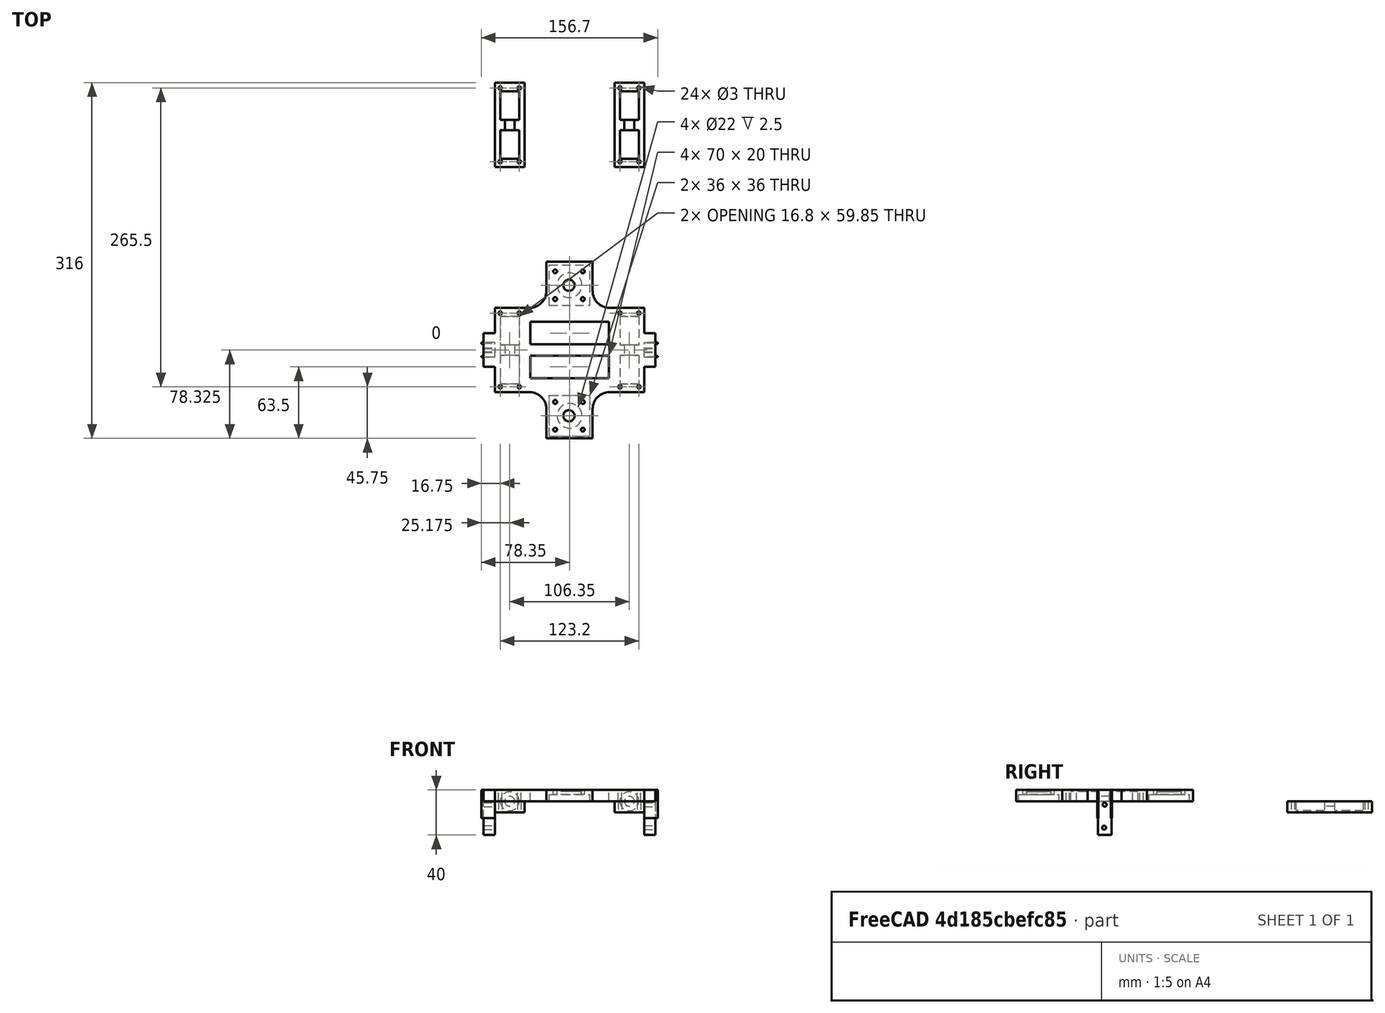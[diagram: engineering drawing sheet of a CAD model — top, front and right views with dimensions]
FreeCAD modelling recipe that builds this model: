
FCSTD DOCUMENT  (FreeCAD 0.16R6712 (Git))
Label: 1.3
License: All rights reserved
LicenseURL: http://en.wikipedia.org/wiki/All_rights_reserved
objects: Part::Cut×24, Part::Cylinder×23, Part::Box×14, Part::MultiFuse×7, Part::FeaturePython×4, Part::Fillet×4, Part::Fuse×2, Part::Feature×2
note: 80 computed .brp shape members not serialized (recipe doc carries the construction recipe); baked Part::Feature solids carry a one-line shape summary decoded from their .brp

FEATURE [Part::Box] Box  label="Cubo"
  Height = 10
  Length = 26.35
  Width = 75
FEATURE [Part::Cylinder] Cylinder  label="Cilindro"
  Angle = 360
  Height = 10
  Placement = pos=(4.75,4.75,0) rot=(0,0,1;0rad)
  Radius = 1.5
FEATURE [Part::Cylinder] Cylinder002  label="Cilindro002"
  Angle = 360
  Height = 10
  Placement = pos=(4.75,70.25,0) rot=(0,0,1;0rad)
  Radius = 1.5
FEATURE [Part::Cylinder] Cylinder003  label="Cilindro003"
  Angle = 360
  Height = 10
  Placement = pos=(21.6,4.75,0) rot=(0,0,1;0rad)
  Radius = 1.5
FEATURE [Part::Cut] Cut
  Base = -> Box
  Tool = -> Cylinder
FEATURE [Part::Cut] Cut001
  Base = -> Cut
  Tool = -> Cylinder002
FEATURE [Part::Cylinder] Cylinder004  label="Cilindro004"
  Angle = 360
  Height = 25.35
  Placement = pos=(13.175,30,0) rot=(1,0,0;1.5708rad)
  Radius = 8.4
FEATURE [Part::Cylinder] Cylinder005  label="Cilindro005"
  Angle = 360
  Height = 25.35
  Placement = pos=(13.175,64.5,0) rot=(1,0,0;1.5708rad)
  Radius = 8.4
FEATURE [Part::Cylinder] Cylinder006  label="Cilindro006"
  Angle = 360
  Height = 9.5
  Placement = pos=(13.175,39.5,0) rot=(1,0,0;1.5708rad)
  Radius = 4.4
FEATURE [Part::Fuse] Fusion
  Base = -> Cylinder004
  Tool = -> Cylinder005
FEATURE [Part::Fuse] Fusion001
  Base = -> Fusion
  Placement = pos=(0,2.75,0) rot=(0,0,1;0rad)
  Tool = -> Cylinder006
FEATURE [Part::Box] Box001  label="Centro"
  Height = 10
  Length = 80
  Placement = pos=(26.35,0,0) rot=(0,0,1;0rad)
  Width = 75
FEATURE [Part::Box] Box002  label="Lucernario"
  Height = 10
  Length = 70
  Placement = pos=(31.35,12.5,0) rot=(0,0,1;0rad)
  Width = 20
FEATURE [Part::Box] Box003  label="Lucernario2"
  Height = 10
  Length = 70
  Placement = pos=(31.35,42.5,0) rot=(0,0,1;0rad)
  Width = 20
FEATURE [Part::Cut] Cut007
  Base = -> Box001
  Tool = -> Box002
FEATURE [Part::Cut] Cut008  label="Centro1"
  Base = -> Cut007
  Tool = -> Box003
FEATURE [Part::Box] Box006  label="Guia1"
  Height = 10
  Length = 10
  Placement = pos=(-10,22.5,0) rot=(0,0,1;0rad)
  Width = 30
FEATURE [Part::Box] Box010  label="Cubo003"
  Height = 10
  Length = 26.35
  Width = 75
FEATURE [Part::Cylinder] Cylinder007  label="Cilindro007"
  Angle = 360
  Height = 25.35
  Placement = pos=(13.175,67.25,0) rot=(1,0,0;1.5708rad)
  Radius = 8.4
FEATURE [Part::Cut] Cut011
  Base = -> Box010
  Tool = -> Cylinder007
FEATURE [Part::Cylinder] Cylinder008  label="Cilindro008"
  Angle = 360
  Height = 9.5
  Placement = pos=(13.175,42.25,0) rot=(1,0,0;1.5708rad)
  Radius = 4.4
FEATURE [Part::Cut] Cut012
  Base = -> Cut011
  Tool = -> Cylinder008
FEATURE [Part::Cylinder] Cylinder009  label="Cilindro009"
  Angle = 360
  Height = 25.35
  Placement = pos=(13.175,32.75,0) rot=(1,0,0;1.5708rad)
  Radius = 8.4
FEATURE [Part::Cut] Cut013
  Base = -> Cut012
  Tool = -> Cylinder009
FEATURE [Part::Cylinder] Cylinder010  label="Cilindro010"
  Angle = 360
  Height = 10
  Placement = pos=(21.6,4.75,0) rot=(0,0,1;0rad)
  Radius = 1.5
FEATURE [Part::Cylinder] Cylinder011  label="Cilindro011"
  Angle = 360
  Height = 10
  Placement = pos=(4.75,4.75,0) rot=(0,0,1;0rad)
  Radius = 1.5
FEATURE [Part::Cut] Cut014
  Base = -> Cut013
  Tool = -> Cylinder010
FEATURE [Part::Cut] Cut015
  Base = -> Cut014
  Tool = -> Cylinder011
FEATURE [Part::Cylinder] Cylinder012  label="Cilindro012"
  Angle = 360
  Height = 10
  Placement = pos=(4.75,70.25,0) rot=(0,0,1;0rad)
  Radius = 1.5
FEATURE [Part::Cylinder] Cylinder013  label="Cilindro013"
  Angle = 360
  Height = 10
  Placement = pos=(21.6,70.25,0) rot=(0,0,1;0rad)
  Radius = 1.5
FEATURE [Part::Cut] Cut016
  Base = -> Cut015
  Tool = -> Cylinder012
FEATURE [Part::Cut] Cut017
  Base = -> Cut016
  Placement = pos=(0,0,0) rot=(0,1,0;3.14159rad)
  Tool = -> Cylinder013
FEATURE [Part::FeaturePython] Array001  label="Cierres"  # Draft array (typed FeaturePython)
  Angle = 360
  ArrayType = 0
  Axis = (0,0,1)
  Base = -> Cut017
  Center = (0,0,0)
  Fuse = false
  IntervalAxis = (0,0,0)
  IntervalX = (106.35,0,0)
  IntervalY = (0,1,0)
  IntervalZ = (0,0,0)
  NumberPolar = 1
  NumberX = 2
  NumberY = 1
  NumberZ = 1
  Placement = pos=(26.35,200,0) rot=(0,0,1;0rad)
FEATURE [Part::Box] Box011  label="Cubo004"
  Height = 10
  Length = 41
  Width = 41
FEATURE [Part::Cylinder] Cylinder014  label="Cilindro014"
  Angle = 360
  Height = 10
  Placement = pos=(7.7,7.7,0) rot=(0,0,1;0rad)
  Radius = 1.7
FEATURE [Part::Cylinder] Cylinder015  label="Cilindro015"
  Angle = 360
  Height = 10
  Placement = pos=(7.7,32.3,0) rot=(0,0,1;0rad)
  Radius = 1.7
FEATURE [Part::Cylinder] Cylinder016  label="Cilindro016"
  Angle = 360
  Height = 10
  Placement = pos=(32.3,7.7,0) rot=(0,0,1;0rad)
  Radius = 1.7
FEATURE [Part::Cylinder] Cylinder017  label="Cilindro017"
  Angle = 360
  Height = 10
  Placement = pos=(32.3,32.3,0) rot=(0,0,1;0rad)
  Radius = 1.7
FEATURE [Part::Cylinder] Cylinder018  label="Cilindro018"
  Angle = 360
  Height = 10
  Placement = pos=(20,20,0) rot=(0,0,1;0rad)
  Radius = 5
FEATURE [Part::Cut] Cut018
  Base = -> Box011
  Tool = -> Cylinder015
FEATURE [Part::Cut] Cut019
  Base = -> Cut018
  Tool = -> Cylinder014
FEATURE [Part::Cut] Cut020
  Base = -> Cut019
  Tool = -> Cylinder016
FEATURE [Part::Cut] Cut021
  Base = -> Cut020
  Tool = -> Cylinder017
FEATURE [Part::Cut] Cut022
  Base = -> Cut021
  Tool = -> Cylinder018
FEATURE [Part::Box] Box012  label="Cubo005"
  Height = 6
  Length = 36
  Placement = pos=(2.5,2,0) rot=(0,0,1;0rad)
  Width = 36
FEATURE [Part::Cut] Cut023
  Base = -> Cut022
  Placement = pos=(43.35,-46,0) rot=(0,0,1;0rad)
  Tool = -> Box012
FEATURE [Part::FeaturePython] Array002  # Draft array (typed FeaturePython)
  Angle = 360
  ArrayType = 0
  Axis = (0,0,1)
  Base = -> Cut023
  Center = (0,0,0)
  Fuse = false
  IntervalAxis = (0,0,0)
  IntervalX = (1,0,0)
  IntervalY = (0,116,0)
  IntervalZ = (0,0,0)
  NumberPolar = 1
  NumberX = 1
  NumberY = 2
  NumberZ = 1
  Placement = pos=(2.5,5,0) rot=(0,0,1;0rad)
FEATURE [Part::Box] Box014  label="Cubo007"
  Height = 25
  Length = 12
  Placement = pos=(132.7,31,-15) rot=(0,0,1;0rad)
  Width = 1
FEATURE [Part::Box] Box015  label="Cubo008"
  Height = 25
  Length = 12
  Placement = pos=(132.7,43,-15) rot=(0,0,1;0rad)
  Width = 1
FEATURE [Part::Box] Box016  label="Cubo009"
  Height = 30
  Length = 10
  Placement = pos=(-10,31.5,-30) rot=(0,0,1;0rad)
  Width = 12
FEATURE [Part::Box] Box017  label="Cubo010"
  Height = 25
  Length = 12
  Placement = pos=(-12,31,-15) rot=(0,0,1;0rad)
  Width = 1
FEATURE [Part::Box] Box018  label="Cubo011"
  Height = 25
  Length = 12
  Placement = pos=(-12,43,-15) rot=(0,0,1;0rad)
  Width = 1
FEATURE [Part::Cylinder] Cylinder019  label="Cilindro019"
  Angle = 360
  Height = 10
  Placement = pos=(-10,37.5,-3) rot=(0,1,0;1.5708rad)
  Radius = 1.75
FEATURE [Part::Cylinder] Cylinder020  label="Cilindro020"
  Angle = 360
  Height = 10
  Placement = pos=(-10,37,-23.5) rot=(0,1,0;1.5708rad)
  Radius = 1.75
FEATURE [Part::Cut] Cut024
  Base = -> Box016
  Tool = -> Cylinder020
FEATURE [Part::Cut] Cut025
  Base = -> Cut024
  Tool = -> Cylinder019
FEATURE [Part::FeaturePython] Array003  # Draft array (typed FeaturePython)
  Angle = 360
  ArrayType = 0
  Axis = (0,0,1)
  Base = -> Cut025
  Center = (0,0,0)
  Fuse = false
  IntervalAxis = (0,0,0)
  IntervalX = (142.7,0,0)
  IntervalY = (0,1,0)
  IntervalZ = (0,0,0)
  NumberPolar = 1
  NumberX = 2
  NumberY = 1
  NumberZ = 1
FEATURE [Part::MultiFuse] Fusion009
  Shapes = -> [Box015,Box014,Array003]
FEATURE [Part::MultiFuse] Fusion010
  Shapes = -> [Fusion009,Box018,Box017]
FEATURE [Part::Box] Box007  label="Guia2"
  Height = 10
  Length = 10
  Placement = pos=(132.7,22.5,0) rot=(0,0,1;0rad)
  Width = 30
FEATURE [Part::Cut] Cut026
  Base = -> Cut001
  Tool = -> Cylinder003
FEATURE [Part::Cylinder] Cylinder021  label="Cilindro021"
  Angle = 360
  Height = 10
  Placement = pos=(21.6,70.25,0) rot=(0,0,1;0rad)
  Radius = 1.5
FEATURE [Part::Cut] Cut027
  Base = -> Cut026
  Tool = -> Cylinder021
FEATURE [Part::Cut] Cut028
  Base = -> Cut027
  Tool = -> Fusion001
FEATURE [Part::FeaturePython] Array  # Draft array (typed FeaturePython)
  Angle = 360
  ArrayType = 0
  Axis = (0,0,1)
  Base = -> Cut028
  Center = (0,0,0)
  Fuse = false
  IntervalAxis = (0,0,0)
  IntervalX = (106.35,0,0)
  IntervalY = (0,1,0)
  IntervalZ = (0,0,0)
  NumberPolar = 1
  NumberX = 2
  NumberY = 1
  NumberZ = 1
FEATURE [Part::MultiFuse] Fusion011
  Shapes = -> [Array,Cut008]
FEATURE [Part::MultiFuse] Fusion012
  Shapes = -> [Array002,Fusion011]
FEATURE [Part::MultiFuse] Fusion013
  Shapes = -> [Fusion010,Fusion012]
FEATURE [Part::MultiFuse] Fusion014
  Shapes = -> [Box007,Fusion013]
FEATURE [Part::MultiFuse] Fusion015
  Shapes = -> [Box006,Fusion014]
FEATURE [Part::Fillet] Fillet
  Base = -> Fusion015
  Edges = 1 edges r=15: [Edge176]
FEATURE [Part::Fillet] Fillet001
  Base = -> Fillet
  Edges = 1 edges r=15: [Edge59]
FEATURE [Part::Fillet] Fillet002
  Base = -> Fillet001
  Edges = 1 edges r=15: [Edge73]
FEATURE [Part::Fillet] Fillet003
  Base = -> Fillet002
  Edges = 1 edges r=15: [Edge61]
FEATURE [Part::Cylinder] Cylinder022  label="Cilindro022"
  Angle = 360
  Height = 2.5
  Placement = pos=(66.35,-21,6) rot=(0,0,1;0rad)
  Radius = 11
FEATURE [Part::Cut] Cut029
  Base = -> Fillet003
  Tool = -> Cylinder022
FEATURE [Part::Cylinder] Cylinder023  label="Cilindro023"
  Angle = 360
  Height = 2.5
  Placement = pos=(66.35,95,6) rot=(0,0,1;0rad)
  Radius = 11
FEATURE [Part::Cut] Cut030
  Base = -> Cut029
  Tool = -> Cylinder023
FEATURE [Part::Feature] Cut030001  label="Cut031"
  shape: bbox 156.7 x 157 x 40 mm, 112 faces (baked)
FEATURE [Part::Feature] Array001001  label="Cierres001"
  shape: bbox 132.7 x 75 x 10 mm, 34 faces, 2 solids (baked)
